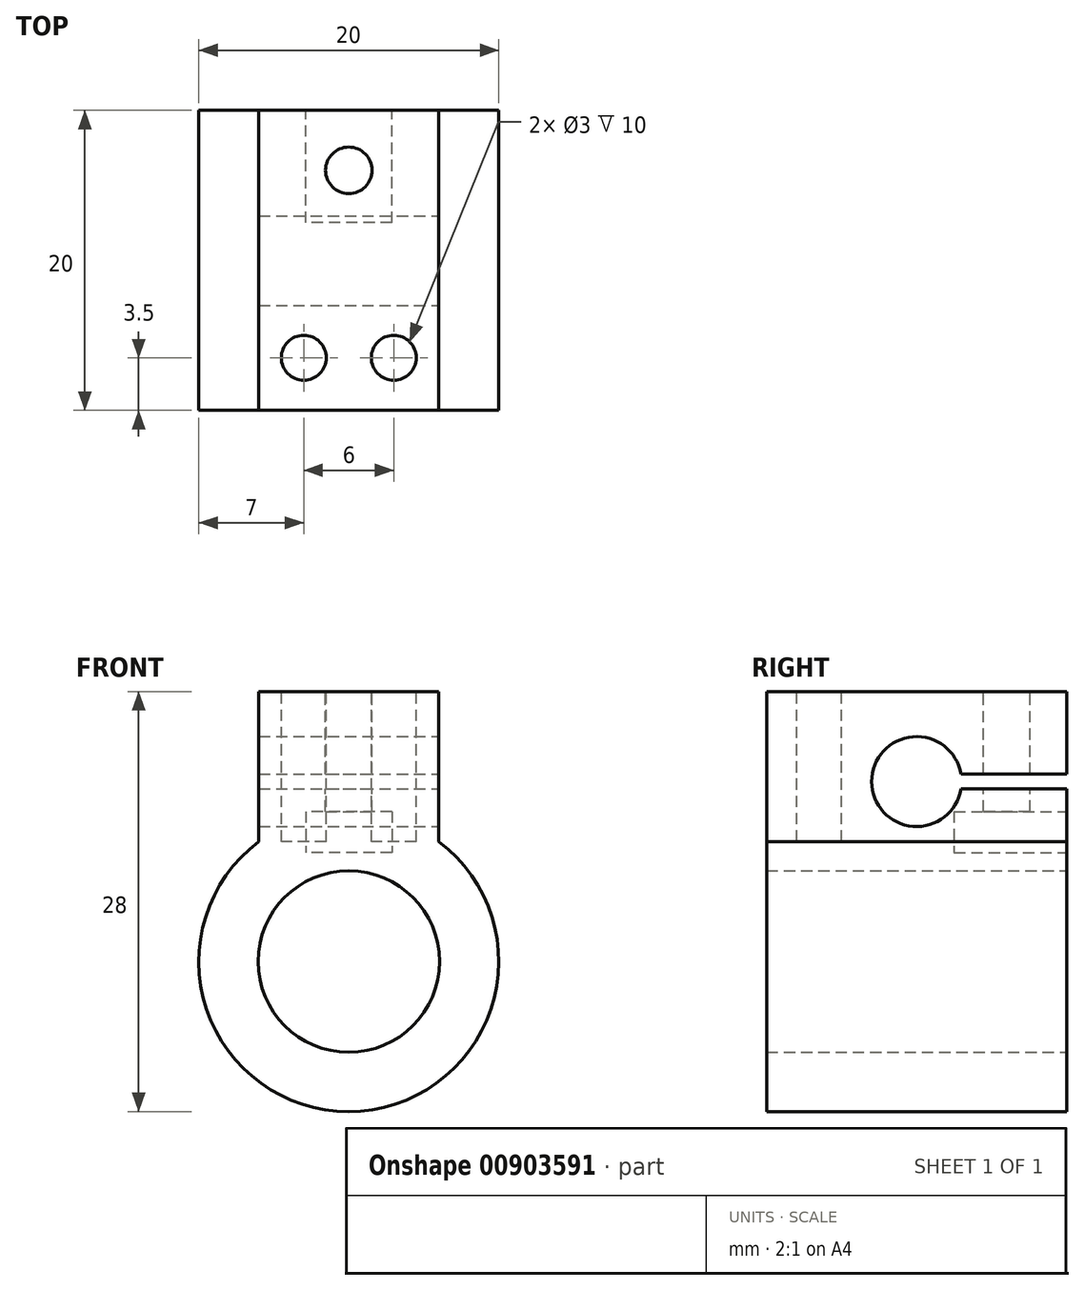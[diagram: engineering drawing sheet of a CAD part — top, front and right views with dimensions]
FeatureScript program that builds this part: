
annotation { "Feature Type Name" : "Feature", "Feature Type Description" : "" }
export const myFeature = defineFeature(function(context is Context, id is Id, definition is map)
    precondition{}
    {
        {
            var Q0;
            Q0=qCreatedBy(makeId("Front.planeOp"),FACE);
            var sketch = newSketch(context, id + "F0", { "sketchPlane" : qUnion([Q0])});
            skLineSegment(sketch, "E0", {"start": v(-6, 8) * mm, "end": v(-6, 18) * mm});
            skLineSegment(sketch, "E1", {"start": v(-6, 18) * mm, "end": v(6, 18) * mm});
            skLineSegment(sketch, "E2", {"start": v(6, 18) * mm, "end": v(6, 8) * mm});
            skCircle(sketch, "E3", {"center": v(0, 0) * mm, "radius": 6.05 * mm});
            skLineSegment(sketch, "E4", {"start": v(0, 0) * mm, "end": v(0, -10) * mm, "construction": true});
            skCircle(sketch, "E5", {"center": v(0, 12) * mm, "radius": 3 * mm, "construction": true});
            skArc(sketch, "E6.trimOffspring", {"start": v(-6, 8) * mm, "mid": v(0, -10) * mm, "end": v(6, 8) * mm});
            skSolve(sketch);
        }
        {
            var Q0;
            Q0=makeQuery(id+"F0.imprint","IMPRINT",FACE,{"disambiguationData":[TD([[makeQuery(id+"F0.imprint","IMPRINT",EDGE,{"derivedFrom":sQuery(id+"F0.wireOp",EDGE,"E0")}),-1.0]])]});
            extrude(context, id + "F1", {"entities" : qUnion([Q0]), "depth" : 20 * mm});
        }
        {
            var Q0;
            Q0=makeQuery(id+"F1.opExtrude","SWEPT_FACE",FACE,{"disambiguationData":[OSD([sQuery(id+"F0.wireOp",EDGE,"E2")])]});
            var sketch = newSketch(context, id + "F2", { "sketchPlane" : qUnion([Q0])});
            skArc(sketch, "E7", {"start": v(-7.04, 12.5) * mm, "mid": v(-13, 12) * mm, "end": v(-7.04, 11.5) * mm});
            skLineSegment(sketch, "E8", {"start": v(-7.04, 12.5) * mm, "end": v(0, 12.5) * mm});
            skLineSegment(sketch, "E9", {"start": v(-7.04, 11.5) * mm, "end": v(0, 11.5) * mm});
            skLineSegment(sketch, "E10", {"start": v(0, 12.5) * mm, "end": v(0, 11.5) * mm});
            skSolve(sketch);
        }
        {
            var Q0;
            Q0=qSketchRegion(id+"F2",true);
            extrude(context, id + "F3", {"entities" : qUnion([Q0]), "operationType" : NewBodyOperationType.REMOVE, "oppositeDirection" : true, "depth" : 25 * mm});
        }
        {
            var Q0;
            {var subQ0=sQuery(id+"F0.wireOp",EDGE,"E6.trimOffspring");var subQ1=sQuery(id+"F0.wireOp",EDGE,"E3");var subQ2=sQuery(id+"F0.wireOp",EDGE,"E2");var subQ3=sQuery(id+"F0.wireOp",EDGE,"E0");Q0=makeQuery(id+"F3.boolean.opBoolean","SPLIT",FACE,{"disambiguationData":[TD([makeQuery(id+"F1.opExtrude","SWEPT_FACE",FACE,{"disambiguationData":[OSD([subQ1])]})])],"derivedFrom":makeQuery(id+"F1.opExtrude","CAP_FACE",FACE,{"disambiguationData":[OSD([subQ3,sQuery(id+"F0.wireOp",EDGE,"E1"),subQ2,subQ1,subQ0,sQuery(id+"F0.wireOp",EDGE,"c32d9758-957b-4987-aa54-74a0080b717f.filletArc"),sQuery(id+"F0.wireOp",EDGE,"a0691a14-58ba-40bc-be37-97391b088e77.filletArc")])],"isStart":true})});}
            var sketch = newSketch(context, id + "F4", { "sketchPlane" : qUnion([Q0])});
            skLineSegment(sketch, "E11.bottom", {"start": v(-2.88, 10) * mm, "end": v(2.87, 10) * mm});
            skLineSegment(sketch, "E11.top", {"start": v(-2.88, 7.25) * mm, "end": v(2.87, 7.25) * mm});
            skLineSegment(sketch, "E11.left", {"start": v(-2.88, 10) * mm, "end": v(-2.88, 7.25) * mm});
            skLineSegment(sketch, "E11.right", {"start": v(2.87, 10) * mm, "end": v(2.87, 7.25) * mm});
            skPoint(sketch, "E12", {"position": v(0, 7.25) * mm});
            skSolve(sketch);
        }
        {
            var Q0;
            Q0=qSketchRegion(id+"F4",true);
            extrude(context, id + "F5", {"entities" : qUnion([Q0]), "operationType" : NewBodyOperationType.REMOVE, "oppositeDirection" : true, "depth" : 7.5 * mm});
        }
        {
            var Q0;
            Q0=makeQuery(id+"F1.opExtrude","SWEPT_FACE",FACE,{"disambiguationData":[OSD([sQuery(id+"F0.wireOp",EDGE,"E1")])]});
            var sketch = newSketch(context, id + "F6", { "sketchPlane" : qUnion([Q0])});
            skCircle(sketch, "E13", {"center": v(0, -4) * mm, "radius": 1.55 * mm});
            skPoint(sketch, "E13.centerSnap0", {"position": v(0, -20) * mm});
            skSolve(sketch);
        }
        {
            var Q0;
            Q0=qSketchRegion(id+"F6",true);
            extrude(context, id + "F7", {"entities" : qUnion([Q0]), "operationType" : NewBodyOperationType.REMOVE, "oppositeDirection" : true, "depth" : 10 * mm});
        }
        {
            var Q0;
            Q0=makeQuery(id+"F1.opExtrude","SWEPT_FACE",FACE,{"disambiguationData":[OSD([sQuery(id+"F0.wireOp",EDGE,"E1")])]});
            var sketch = newSketch(context, id + "F8", { "sketchPlane" : qUnion([Q0])});
            skCircle(sketch, "E14.cCircle", {"center": v(0, -4) * mm, "radius": 2.75 * mm, "construction": true});
            skLineSegment(sketch, "E14.0", {"start": v(0, -7.18) * mm, "end": v(-2.75, -5.59) * mm});
            skLineSegment(sketch, "E14.1", {"start": v(-2.75, -5.59) * mm, "end": v(-2.75, -2.41) * mm});
            skLineSegment(sketch, "E14.2", {"start": v(-2.75, -2.41) * mm, "end": v(0, -0.82) * mm});
            skLineSegment(sketch, "E14.3", {"start": v(0, -0.82) * mm, "end": v(2.75, -2.41) * mm});
            skLineSegment(sketch, "E14.4", {"start": v(2.75, -2.41) * mm, "end": v(2.75, -5.59) * mm});
            skLineSegment(sketch, "E14.5", {"start": v(2.75, -5.59) * mm, "end": v(0, -7.18) * mm});
            skPoint(sketch, "E14.0.midPoint", {"position": v(-1.37, -6.38) * mm});
            skSolve(sketch);
        }
        {
            var Q0;
            Q0=makeQuery(id+"F8.imprint","IMPRINT",FACE,{"disambiguationData":[TD([[makeQuery(id+"F8.imprint","IMPRINT",EDGE,{"derivedFrom":sQuery(id+"F8.wireOp",EDGE,"E14.0")}),1.0]])]});
            var sketch = newSketch(context, id + "F9", { "sketchPlane" : qUnion([Q0])});
            skCircle(sketch, "E15", {"center": v(-3, -16.5) * mm, "radius": 1.5 * mm});
            skCircle(sketch, "E16", {"center": v(3, -16.5) * mm, "radius": 1.5 * mm});
            skLineSegment(sketch, "E17", {"start": v(3, -16.5) * mm, "end": v(0, -16.5) * mm, "construction": true});
            skLineSegment(sketch, "E18", {"start": v(0, -16.5) * mm, "end": v(-3, -16.5) * mm, "construction": true});
            skSolve(sketch);
        }
        {
            var Q0;
            Q0=qSketchRegion(id+"F9",true);
            extrude(context, id + "F10", {"entities" : qUnion([Q0]), "operationType" : NewBodyOperationType.REMOVE, "oppositeDirection" : true, "depth" : 10 * mm});
        }
    });
